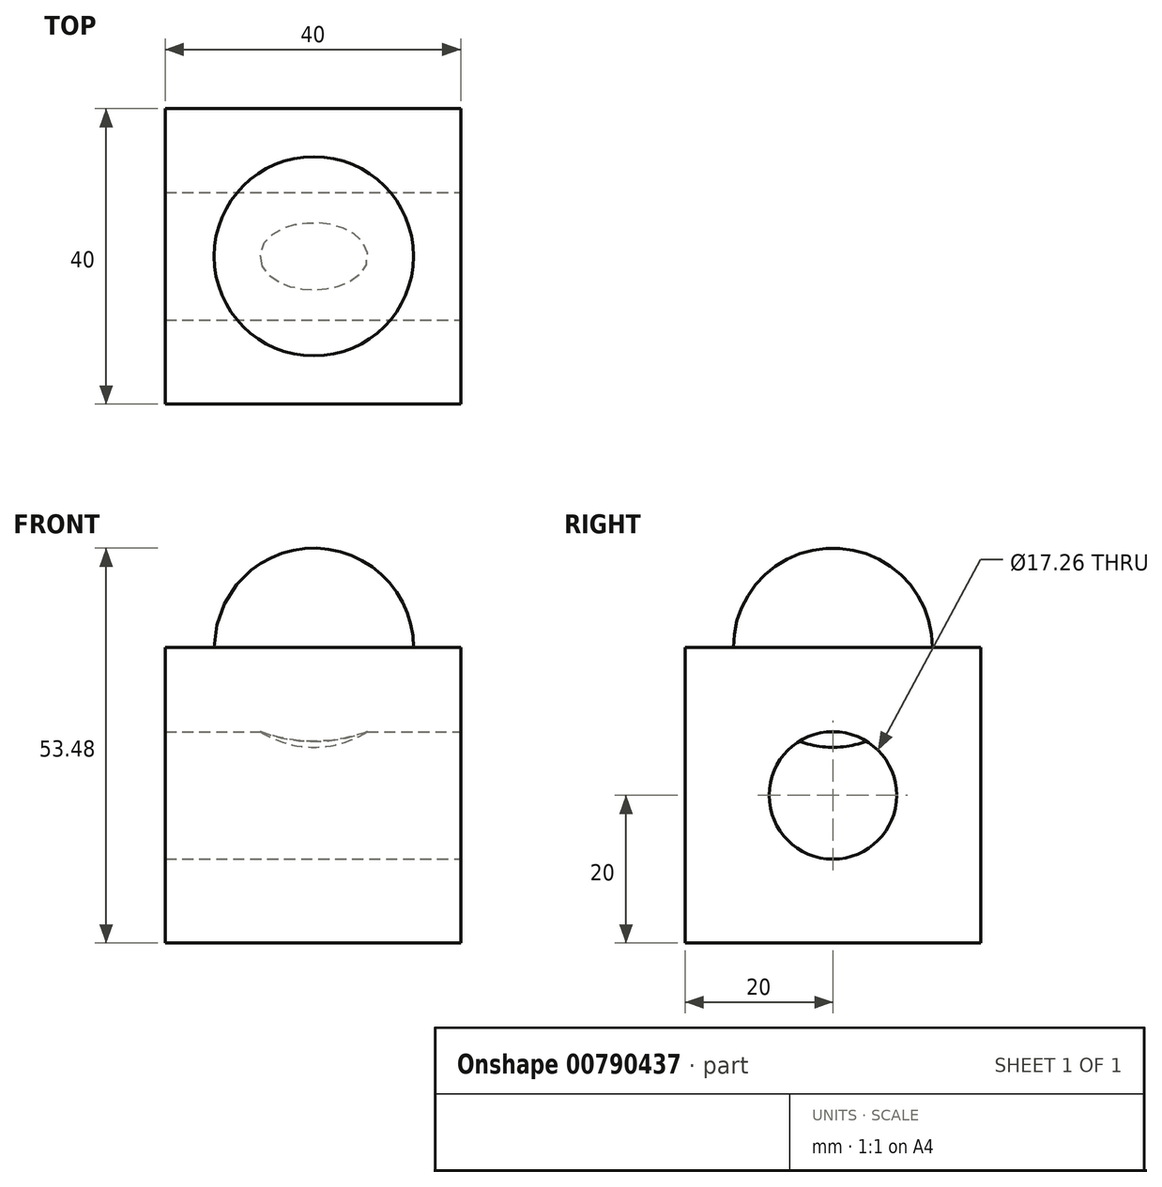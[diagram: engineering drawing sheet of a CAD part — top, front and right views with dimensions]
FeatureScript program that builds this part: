
annotation { "Feature Type Name" : "Feature", "Feature Type Description" : "" }
export const myFeature = defineFeature(function(context is Context, id is Id, definition is map)
    precondition{}
    {
        {
            var Q0;
            Q0=qCreatedBy(makeId("Front.planeOp"),FACE);
            var sketch = newSketch(context, id + "F0", { "sketchPlane" : qUnion([Q0])});
            skLineSegment(sketch, "E0.bottom", {"start": v(0, 0) * mm, "end": v(40, 0) * mm});
            skLineSegment(sketch, "E0.top", {"start": v(0, 40) * mm, "end": v(40, 40) * mm});
            skLineSegment(sketch, "E0.left", {"start": v(0, 0) * mm, "end": v(0, 40) * mm});
            skLineSegment(sketch, "E0.right", {"start": v(40, 0) * mm, "end": v(40, 40) * mm});
            skSolve(sketch);
        }
        {
            var Q0;
            Q0 = qSketchRegion(id + "F0", true);
            extrude(context, id + "F1", {"entities" : qUnion([Q0]), "depth" : 40 * mm, "offsetDistance" : 25 * mm});
        }
        {
            var Q0;
            Q0=makeQuery(id+"F1.opExtrude","SWEPT_FACE",FACE,{"disambiguationData":[OSD([sQuery(id+"F0.wireOp",EDGE,"E0.right")])]});
            var sketch = newSketch(context, id + "F2", { "sketchPlane" : qUnion([Q0])});
            skCircle(sketch, "E1", {"center": v(-20, 20) * mm, "radius": 8.63 * mm});
            skPoint(sketch, "E1.centerSnap0", {"position": v(0, 20) * mm});
            skPoint(sketch, "E1.centerSnap1", {"position": v(-20, 40) * mm});
            skSolve(sketch);
        }
        {
            var Q0;
            Q0 = qSketchRegion(id + "F2", true);
            extrude(context, id + "F3", {"entities" : qUnion([Q0]), "operationType" : NewBodyOperationType.REMOVE, "endBound" : BoundingType.THROUGH_ALL, "oppositeDirection" : true, "depth" : 25 * mm, "offsetDistance" : 25 * mm});
        }
        {
            var Q0;
            Q0=makeQuery(id+"F1.opExtrude","SWEPT_FACE",FACE,{"disambiguationData":[OSD([sQuery(id+"F0.wireOp",EDGE,"E0.top")])]});
            var sketch = newSketch(context, id + "F4", { "sketchPlane" : qUnion([Q0])});
            skLineSegment(sketch, "E2", {"start": v(6.62, -20) * mm, "end": v(33.6, -20) * mm});
            skPoint(sketch, "E2.startSnap0", {"position": v(0, -20) * mm});
            skArc(sketch, "E3", {"start": v(33.6, -20) * mm, "mid": v(20.11, -6.52) * mm, "end": v(6.62, -20) * mm});
            skSolve(sketch);
        }
        {
            var Q0;
            Q0 = qSketchRegion(id + "F4", true);
            var Q1;
            Q1=sQuery(id+"F4.wireOp",EDGE,"E2");
            revolve(context, id + "F5", {"operationType" : NewBodyOperationType.ADD, "surfaceOperationType" : NewSurfaceOperationType.NEW, "entities" : qUnion([Q0]), "axis" : qUnion([Q1]), "revolveType" : RevolveType.FULL});
        }
    });
